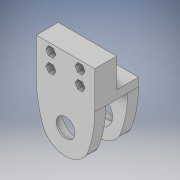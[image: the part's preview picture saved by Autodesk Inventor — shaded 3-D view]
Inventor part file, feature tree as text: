
AUTODESK INVENTOR PART (.ipt)
format: ipt  version: 2019 (Build 230136000, 136)  size: 314,368 bytes
history: native  units: mm
features: sketch x13, extrude x10, chamfer x5, hole x3, plane x1, fillet x1
ambient origin geometry x8: Origin, YZ Plane, XZ Plane, XY Plane, X Axis, Y Axis, Z Axis, Center Point
bodies: Solid1 (feature_tree)
feature tree (33):
  extrude  "Extrusion1"  Depth=20.0mm
  extrude  "Extrusion2"  Depth=40.0mm
  hole  "Hole1"  [1 undecoded]
  plane  "Work Plane1"
  extrude  "Extrusion3"  Depth=30.0mm TaperAngle=360.0deg
  extrude  "Extrusion4"  Depth=15.0mm TaperAngle=0.0deg
  hole  "Hole2"  [1 undecoded]
  extrude  "Extrusion5"  Depth=10.0mm
  extrude  "Extrusion6"  Depth=5.9mm
  chamfer  "Chamfer2"  Distance=3.5mm
  fillet  "Fillet1"  Radius=17.0mm
  extrude  "Extrusion7"  Depth=10.0mm TaperAngle=45.0deg
  chamfer  "Chamfer3"  Distance=10.0mm
  chamfer  "Chamfer4"  Distance=9.17mm Angle=45.0deg
  extrude  "Extrusion8"  Depth=4.0mm TaperAngle=45.0deg
  extrude  "Extrusion9"  Depth=1.0mm TaperAngle=0.0deg
  chamfer  "Chamfer5"  Distance=1.0mm
  hole  "Hole3"  [1 undecoded]
  extrude  "Extrusion10"  Depth=10.0mm
  chamfer  "Chamfer6"  Distance=10.0mm
  sketch  "Sketch1"  dims[d0=19.5mm d2=20.0mm]
  sketch  "Sketch2"  dims[d3=45.0mm d4=40.0mm]
  sketch  "Sketch3"  dims[d5=30.0mm d6=0.0mm d7=27.0mm]
  sketch  "Sketch4"  dims[d8=6.0mm d9=30.0mm d11=360.0deg]
  sketch  "Sketch5"  dims[d13=3.5mm d14=0.0mm]
  sketch  "Sketch6"  dims[d15=3.9mm d16=6.0mm d17=5.0mm d18=5.0mm d19=90.0deg d20=10.0mm d21=0.0mm d22=15.0mm d23=0.0mm]
  sketch  "Sketch7"  dims[d27=20.0mm d28=15.0mm d29=0.0mm]
  sketch  "Sketch8"  dims[d30=20.0mm]
  sketch  "Sketch10"  dims[d31=3.75mm d32=6.0mm d33=4.0mm d34=2.0mm d35=90.0deg d36=10.0mm d37=90.0deg d38=5.9mm]
  sketch  "Sketch11"  dims[d39=5.9mm d40=5.9mm]
  sketch  "Sketch12"  dims[d41=5.9mm d42=3.5mm d43=0.0mm d44=17.0mm]
  sketch  "Sketch13"  dims[d45=10.0mm d46=0.0mm d47=8.25mm d48=2.0mm d49=45.0deg]
  sketch  "Sketch14"  dims[d50=74.25mm d51=10.0mm d52=0.0mm d53=9.17mm d54=2.0mm d55=45.0deg d56=4.0mm d57=2.0mm d58=45.0deg d59=1.0mm d60=0.0mm d61=1.0mm d62=0.0mm d63=2.0mm d64=2.0mm d65=45.0deg d66=13.0mm d67=6.0mm d68=10.0mm d69=7.0mm d70=90.0deg d71=8.0mm d72=20.594885mm d73=1.5mm d74=10.0mm d75=0.0mm d76=4.66mm d77=2.0mm d78=45.0deg]
note: 3 required parameter values undecoded (feature->parameter linkage not recoverable at this tier; creation-order binding heuristic only, values carry confidence <= 0.55)
